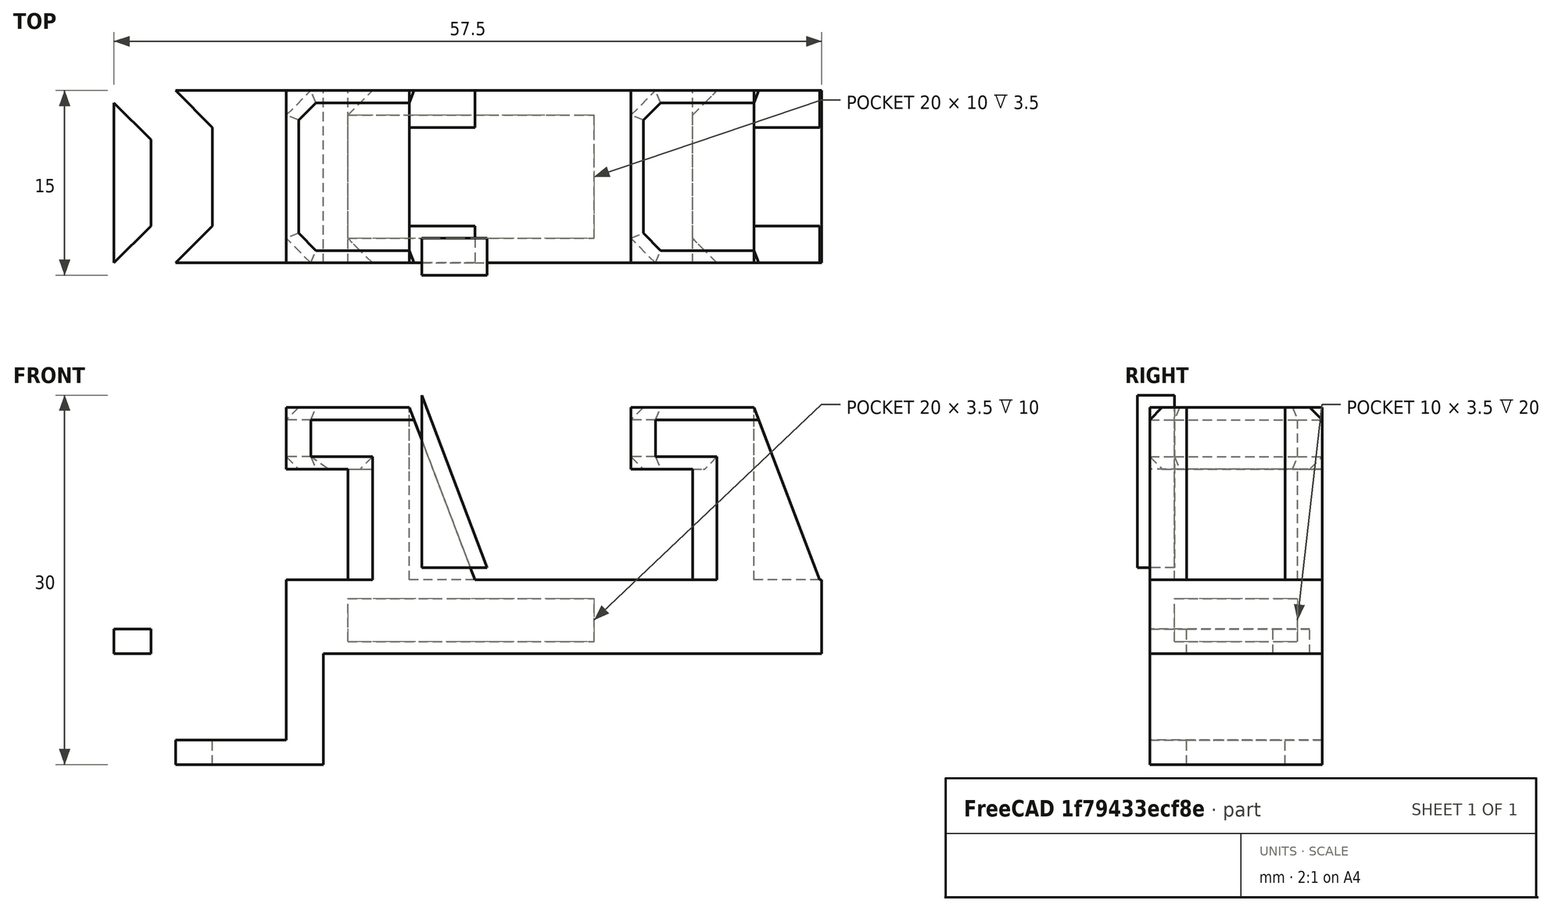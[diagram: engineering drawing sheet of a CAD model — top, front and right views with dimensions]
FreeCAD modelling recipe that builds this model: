
FCSTD DOCUMENT  (FreeCAD 0.18R14555 (Git shallow))
Label: hanger
License: All rights reserved
LicenseURL: http://en.wikipedia.org/wiki/All_rights_reserved
objects: Part::Box×8, Part::Feature×8, Sketcher::SketchObject×2, PartDesign::Pad×2, PartDesign::Body×2, Part::MultiFuse×2, Part::Cut×2, Part::Chamfer×2
note: 30 computed .brp shape members not serialized (recipe doc carries the construction recipe); baked Part::Feature solids carry a one-line shape summary decoded from their .brp

FEATURE [Part::Box] Box  label="Cube"
  AttacherType = Attacher::AttachEngine3D
  Height = 3.5
  Length = 20
  Placement = pos=(0,0,1) rot=(0,0,1;0rad)
  Width = 10
FEATURE [Part::Box] Box001  label="Cube001"
  AttacherType = Attacher::AttachEngine3D
  Height = 6
  Length = 40.5
  Placement = pos=(-2,-2,0) rot=(0,0,1;0rad)
  Width = 14
FEATURE [Part::Box] Box002  label="Cube002"
  AttacherType = Attacher::AttachEngine3D
  Height = 15
  Length = 3
  Placement = pos=(-5,-2,-9) rot=(0,0,1;0rad)
  Width = 14
FEATURE [Part::Box] Box003  label="Cube003"
  AttacherType = Attacher::AttachEngine3D
  Height = 2
  Length = 12
  Placement = pos=(-14,-2,-9) rot=(0,0,1;0rad)
  Width = 14
FEATURE [Sketcher::SketchObject] Sketch
  MapMode = 5
  Support = -> [XY_Plane]
  sketch-geometry (4):
    g0: LineSegment StartX=-19 StartY=11 StartZ=0 EndX=-19 EndY=-2 EndZ=0
    g1: LineSegment StartX=-19 StartY=-2 StartZ=0 EndX=-16 EndY=1 EndZ=0
    g2: LineSegment StartX=-16 StartY=1 StartZ=0 EndX=-16 EndY=8 EndZ=0
    g3: LineSegment StartX=-16 StartY=8 StartZ=0 EndX=-19 EndY=11 EndZ=0
  constraints (5):
    c: Vertical(g0)
    c: Coincident(g0,g1)
    c: Coincident(g1,g2)
    c: Vertical(g2)
    c: Coincident(g2,g3)
FEATURE [PartDesign::Pad] Pad
  Length = 2
  Length2 = 100
  Profile = -> Sketch
  Type = 0
FEATURE [PartDesign::Body] Body
  Group = -> [Sketch,Pad]
  Origin = -> Origin
  Tip = -> Pad
FEATURE [Part::Feature] Body001
  Placement = pos=(5,0,-9) rot=(0,0,1;0rad)
  shape: bbox 3 x 13 x 2 mm, 6 faces (baked)
FEATURE [Part::Feature] Body002
  Placement = pos=(5,1,-9) rot=(0,0,1;0rad)
  shape: bbox 3 x 13 x 2 mm, 6 faces (baked)
FEATURE [Part::MultiFuse] Fusion
  Shapes = -> [Body002,Body001]
FEATURE [Part::Cut] Cut
  Base = -> Box003
  Tool = -> Fusion
FEATURE [Part::Box] Box004  label="Cube004"
  AttacherType = Attacher::AttachEngine3D
  Height = 20
  Length = 5
  Placement = pos=(0,-2,0) rot=(0,0,1;0rad)
  Width = 14
FEATURE [Part::Box] Box005  label="Cube005"
  AttacherType = Attacher::AttachEngine3D
  Height = 20
  Length = 5
  Placement = pos=(28,-2,0) rot=(0,0,1;0rad)
  Width = 14
FEATURE [Part::Box] Box006  label="Cube006"
  AttacherType = Attacher::AttachEngine3D
  Height = 5
  Length = 10
  Placement = pos=(-5,-2,15) rot=(0,0,1;0rad)
  Width = 14
FEATURE [Part::Box] Box007  label="Cube007"
  AttacherType = Attacher::AttachEngine3D
  Height = 5
  Length = 10
  Placement = pos=(23,-2,15) rot=(0,0,1;0rad)
  Width = 14
FEATURE [Sketcher::SketchObject] Sketch001
  MapMode = 5
  Placement = pos=(0,0,0) rot=(1,0,0;1.5708rad)
  Support = -> [XZ_Plane001]
  sketch-geometry (3):
    g0: LineSegment StartX=6 StartY=7 StartZ=0 EndX=6 EndY=21 EndZ=0
    g1: LineSegment StartX=6 StartY=21 StartZ=0 EndX=11.3253 EndY=7 EndZ=0
    g2: LineSegment StartX=11.3253 StartY=7 StartZ=0 EndX=6 EndY=7 EndZ=0
  constraints (5):
    c: Vertical(g0)
    c: Coincident(g0,g1)
    c: Coincident(g1,g2)
    c: Coincident(g2,g0)
    c: Horizontal(g2)
FEATURE [PartDesign::Pad] Pad001
  Length = 3
  Length2 = 100
  Placement = pos=(0,0,0) rot=(1,0,0;1.5708rad)
  Profile = -> Sketch001
  Type = 0
FEATURE [PartDesign::Body] Body003
  Group = -> [Sketch001,Pad001]
  Origin = -> Origin001
  Tip = -> Pad001
FEATURE [Part::Feature] Body003001  label="Body004"
  Placement = pos=(-1,12,-1) rot=(0,0,1;0rad)
  shape: bbox 5.325 x 3 x 14 mm, 5 faces (baked)
FEATURE [Part::Feature] Body003002  label="Body005"
  Placement = pos=(-1,1,-1) rot=(0,0,1;0rad)
  shape: bbox 5.325 x 3 x 14 mm, 5 faces (baked)
FEATURE [Part::Feature] Body003003  label="Body006"
  Placement = pos=(27,12,-1) rot=(0,0,1;0rad)
  shape: bbox 5.325 x 3 x 14 mm, 5 faces (baked)
FEATURE [Part::Feature] Body003004  label="Body007"
  Placement = pos=(27,1,-1) rot=(0,0,1;0rad)
  shape: bbox 5.325 x 3 x 14 mm, 5 faces (baked)
FEATURE [Part::MultiFuse] Fusion001
  Shapes = -> [Box001,Box002,Box005,Body003004,Cut,Box004,Body003001,Body003003,Box006,Box007,Body003002]
FEATURE [Part::Feature] Fusion001001  label="Fusion002"
  shape: bbox 52.5 x 14 x 29 mm, 32 faces (baked)
FEATURE [Part::Chamfer] Chamfer
  Base = -> Fusion001001
  Edges = 8 edges r=2: [Edge22,Edge24,Edge28,Edge30,Edge52,Edge56,Edge58,Edge63]
FEATURE [Part::Chamfer] Chamfer001
  Base = -> Chamfer
  Edges = 19 edges r=1: [Edge1,Edge4,Edge16,Edge20,Edge25,Edge26,Edge28,Edge30,Edge32,Edge36,Edge37,Edge39,Edge74,Edge75,Edge77,Edge79,Edge84,Edge89,Edge91]
FEATURE [Part::Feature] Chamfer001001  label="Chamfer002"
  shape: bbox 52.5 x 14 x 29 mm, 59 faces (baked)
FEATURE [Part::Cut] Cut001
  Base = -> Chamfer001001
  Tool = -> Box
